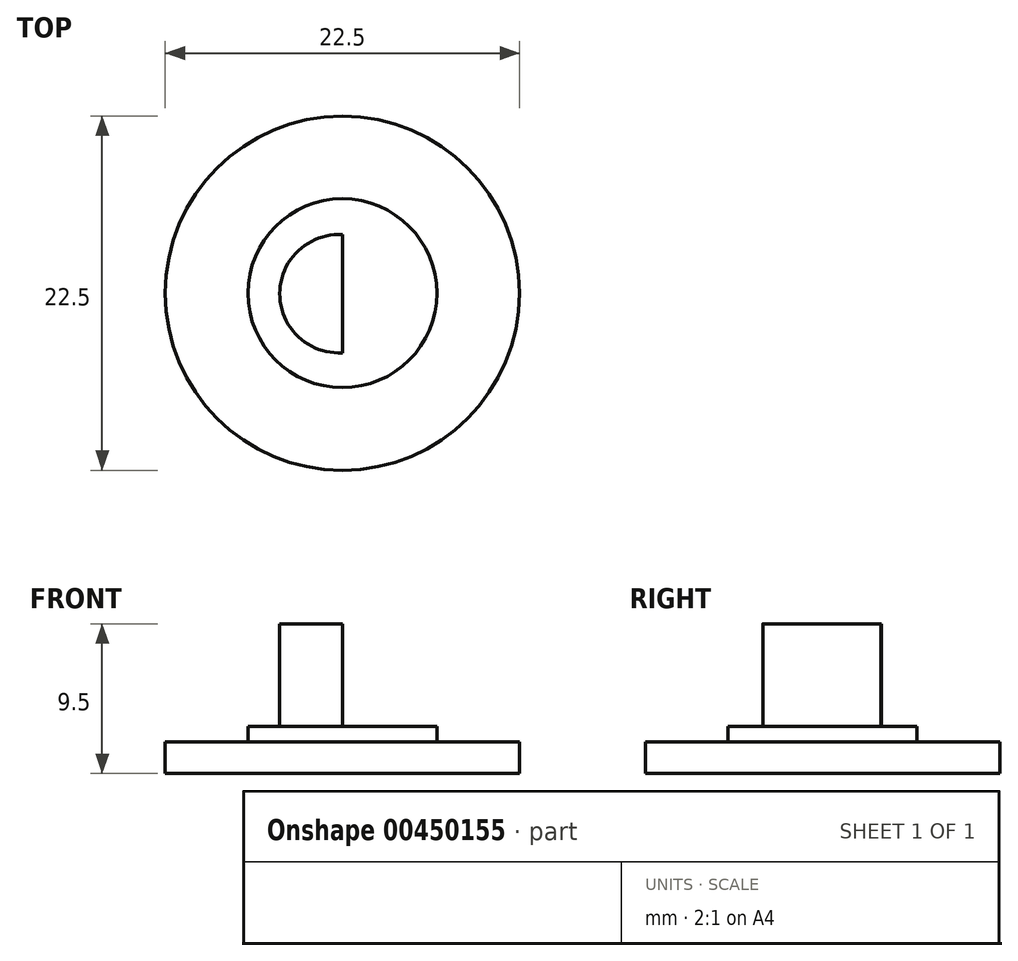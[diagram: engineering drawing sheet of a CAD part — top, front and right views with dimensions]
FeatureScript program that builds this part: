
annotation { "Feature Type Name" : "Feature", "Feature Type Description" : "" }
export const myFeature = defineFeature(function(context is Context, id is Id, definition is map)
    precondition{}
    {
        {
            var Q0;
            Q0=qCreatedBy(makeId("Top.planeOp"),FACE);
            var sketch = newSketch(context, id + "F0", { "sketchPlane" : qUnion([Q0])});
            skCircle(sketch, "E0", {"center": v(0, 0) * mm, "radius": 11.25 * mm});
            skSolve(sketch);
        }
        {
            var Q0;
            Q0 = qSketchRegion(id + "F0", true);
            extrude(context, id + "F1", {"entities" : qUnion([Q0]), "depth" : 2 * mm, "offsetDistance" : 25 * mm});
        }
        {
            var Q0;
            Q0=makeQuery(id+"F1.opExtrude","CAP_FACE",FACE,{"disambiguationData":[OSD([sQuery(id+"F0.wireOp",EDGE,"E0")])],"isStart":false});
            var sketch = newSketch(context, id + "F2", { "sketchPlane" : qUnion([Q0])});
            skCircle(sketch, "E1", {"center": v(0, 0) * mm, "radius": 6 * mm});
            skSolve(sketch);
        }
        {
            var Q0;
            Q0 = qSketchRegion(id + "F2", true);
            extrude(context, id + "F3", {"entities" : qUnion([Q0]), "operationType" : NewBodyOperationType.ADD, "depth" : 1 * mm, "offsetDistance" : 25 * mm});
        }
        {
            var Q0;
            Q0=makeQuery(id+"F3.opExtrude","CAP_FACE",FACE,{"disambiguationData":[OSD([sQuery(id+"F2.wireOp",EDGE,"E1")])],"isStart":false});
            var sketch = newSketch(context, id + "F4", { "sketchPlane" : qUnion([Q0])});
            skSolve(sketch);
        }
        {
            var Q0;
            Q0=makeQuery(id+"F4.imprint","IMPRINT",FACE,{"disambiguationData":[TD([[makeQuery(id+"F4.imprint","IMPRINT",EDGE,{"derivedFrom":makeQuery(id+"F3.opExtrude","CAP_EDGE",EDGE,{"disambiguationData":[OSD([sQuery(id+"F2.wireOp",EDGE,"E1")])],"isStart":false})}),1.0]])]});
            var sketch = newSketch(context, id + "F5", { "sketchPlane" : qUnion([Q0])});
            skLineSegment(sketch, "E2", {"start": v(0, -3.78) * mm, "end": v(0, 3.72) * mm});
            skArc(sketch, "E3", {"start": v(0, 3.72) * mm, "mid": v(-3.98, -0.03) * mm, "end": v(0, -3.78) * mm});
            skSolve(sketch);
        }
        {
            var Q0;
            Q0 = qSketchRegion(id + "F5", true);
            extrude(context, id + "F6", {"entities" : qUnion([Q0]), "operationType" : NewBodyOperationType.ADD, "depth" : 6.5 * mm, "offsetDistance" : 25 * mm});
        }
        {
            var Q0;
            Q0 = qSketchRegion(id + "F5", true);
            extrude(context, id + "F7", {"entities" : qUnion([Q0]), "operationType" : NewBodyOperationType.ADD, "depth" : 6 * mm, "offsetDistance" : 25 * mm});
        }
    });
